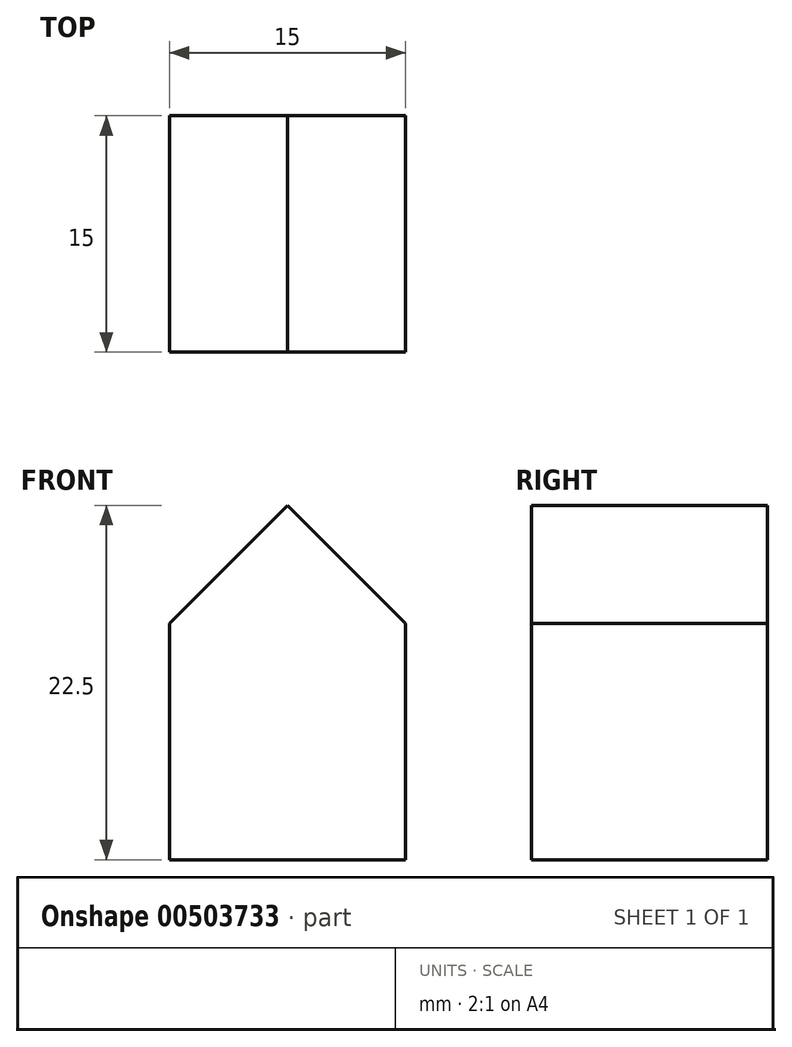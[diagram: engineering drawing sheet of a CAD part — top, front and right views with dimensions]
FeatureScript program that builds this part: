
annotation { "Feature Type Name" : "Feature", "Feature Type Description" : "" }
export const myFeature = defineFeature(function(context is Context, id is Id, definition is map)
    precondition{}
    {
        {
            var Q0;
            Q0=qCreatedBy(makeId("Top.planeOp"),FACE);
            var sketch = newSketch(context, id + "F0", { "sketchPlane" : qUnion([Q0])});
            skLineSegment(sketch, "E0.bottom", {"start": v(0, 0) * mm, "end": v(15, 0) * mm});
            skLineSegment(sketch, "E0.top", {"start": v(0, -15) * mm, "end": v(15, -15) * mm});
            skLineSegment(sketch, "E0.left", {"start": v(0, 0) * mm, "end": v(0, -15) * mm});
            skLineSegment(sketch, "E0.right", {"start": v(15, 0) * mm, "end": v(15, -15) * mm});
            skSolve(sketch);
        }
        {
            var Q0;
            Q0=makeQuery(id+"F0.imprint","IMPRINT",FACE,{"disambiguationData":[TD([[makeQuery(id+"F0.imprint","IMPRINT",EDGE,{"derivedFrom":sQuery(id+"F0.wireOp",EDGE,"E0.bottom")}),-1.0]])]});
            extrude(context, id + "F1", {"entities" : qUnion([Q0]), "depth" : 15 * mm});
        }
        {
            var Q0;
            Q0=makeQuery(id+"F1.opExtrude","SWEPT_FACE",FACE,{"disambiguationData":[OSD([sQuery(id+"F0.wireOp",EDGE,"E0.top")])]});
            var sketch = newSketch(context, id + "F2", { "sketchPlane" : qUnion([Q0])});
            skLineSegment(sketch, "E1", {"start": v(0, 15) * mm, "end": v(7.5, 22.5) * mm});
            skPoint(sketch, "E1.endSnap0", {"position": v(7.5, 0) * mm});
            skLineSegment(sketch, "E2", {"start": v(7.5, 22.5) * mm, "end": v(15, 15) * mm});
            skSolve(sketch);
        }
        {
            var Q0;
            Q0=makeQuery(id+"F2.imprint","IMPRINT",FACE,{"disambiguationData":[TD([[makeQuery(id+"F2.imprint","IMPRINT",EDGE,{"derivedFrom":sQuery(id+"F2.wireOp",EDGE,"E1")}),-1.0]])]});
            extrude(context, id + "F3", {"entities" : qUnion([Q0]), "operationType" : NewBodyOperationType.ADD, "depth" : -15 * mm});
        }
    });
